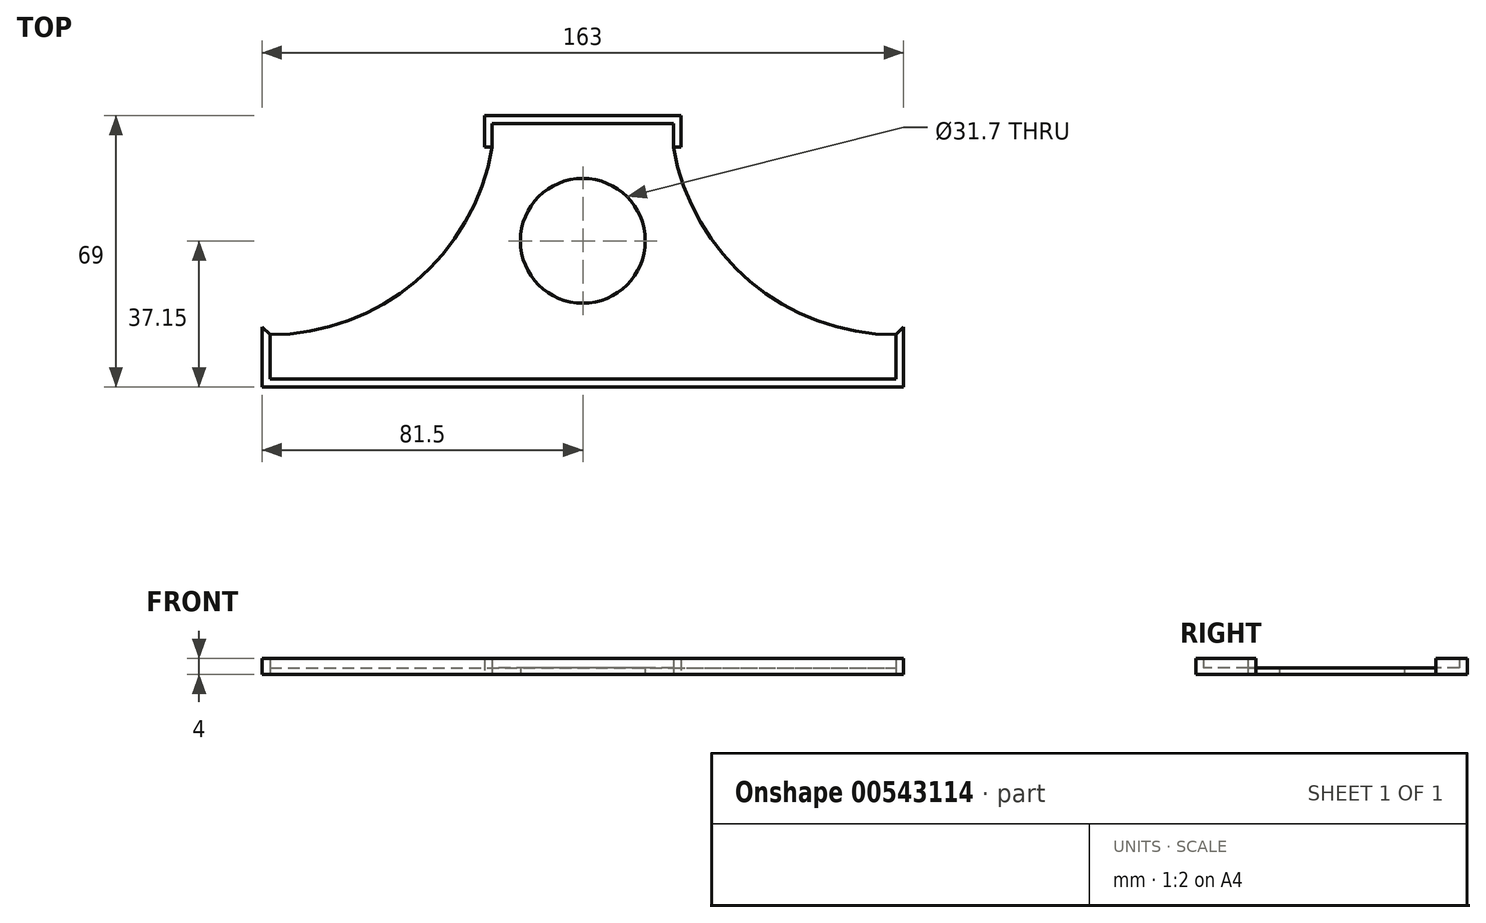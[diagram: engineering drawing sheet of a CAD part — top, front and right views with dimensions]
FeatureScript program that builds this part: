
annotation { "Feature Type Name" : "Feature", "Feature Type Description" : "" }
export const myFeature = defineFeature(function(context is Context, id is Id, definition is map)
    precondition{}
    {
        {
            var Q0;
            Q0=qCreatedBy(makeId("Top.planeOp"),FACE);
            var sketch = newSketch(context, id + "F0", { "sketchPlane" : qUnion([Q0])});
            skLineSegment(sketch, "E0", {"start": v(0, 0) * mm, "end": v(0, 5.65) * mm});
            skLineSegment(sketch, "E1", {"start": v(-79.5, 5.65) * mm, "end": v(79.5, 5.65) * mm});
            skLineSegment(sketch, "E2", {"start": v(-79.5, -5.65) * mm, "end": v(79.5, -5.65) * mm});
            skLineSegment(sketch, "E3", {"start": v(79.5, -5.65) * mm, "end": v(79.5, 5.65) * mm});
            skLineSegment(sketch, "E4", {"start": v(-79.5, 5.65) * mm, "end": v(-79.5, -5.65) * mm});
            skPoint(sketch, "E5", {"position": v(0, 59.35) * mm});
            skLineSegment(sketch, "E6", {"start": v(23, 59.35) * mm, "end": v(-23, 59.35) * mm});
            skLineSegment(sketch, "E7", {"start": v(-23, 53.35) * mm, "end": v(23, 53.35) * mm});
            skArc(sketch, "E8", {"start": v(-79.5, 5.65) * mm, "mid": v(-42.53, 19.17) * mm, "end": v(-23, 53.35) * mm});
            skArc(sketch, "E9", {"start": v(23, 53.35) * mm, "mid": v(42.53, 19.17) * mm, "end": v(79.5, 5.65) * mm});
            skLineSegment(sketch, "E10", {"start": v(-23, 59.35) * mm, "end": v(-23, 53.35) * mm});
            skLineSegment(sketch, "E11", {"start": v(23, 59.35) * mm, "end": v(23, 53.35) * mm});
            skLineSegment(sketch, "E12.0", {"start": v(23, 61.35) * mm, "end": v(-23, 61.35) * mm});
            skLineSegment(sketch, "E13", {"start": v(-23, 61.35) * mm, "end": v(-23, 59.35) * mm});
            skLineSegment(sketch, "E14", {"start": v(23, 61.35) * mm, "end": v(23, 59.35) * mm});
            skLineSegment(sketch, "E15.0", {"start": v(-25, 59.35) * mm, "end": v(-25, 53.35) * mm});
            skLineSegment(sketch, "E15.1", {"start": v(-25, 61.35) * mm, "end": v(-25, 59.35) * mm});
            skLineSegment(sketch, "E16.0", {"start": v(25, 59.35) * mm, "end": v(25, 53.35) * mm});
            skLineSegment(sketch, "E16.1", {"start": v(25, 61.35) * mm, "end": v(25, 59.35) * mm});
            skLineSegment(sketch, "E17", {"start": v(-25, 61.35) * mm, "end": v(-23, 61.35) * mm});
            skLineSegment(sketch, "E18", {"start": v(25, 61.35) * mm, "end": v(23, 61.35) * mm});
            skLineSegment(sketch, "E19.0", {"start": v(81.5, -7.65) * mm, "end": v(81.5, 7.66) * mm});
            skLineSegment(sketch, "E19.1", {"start": v(-81.5, -7.65) * mm, "end": v(81.5, -7.65) * mm});
            skLineSegment(sketch, "E19.2", {"start": v(-81.5, 7.66) * mm, "end": v(-81.5, -7.65) * mm});
            skLineSegment(sketch, "E20", {"start": v(-81.5, 7.66) * mm, "end": v(-79.5, 5.65) * mm});
            skLineSegment(sketch, "E21", {"start": v(79.5, 5.65) * mm, "end": v(81.5, 7.66) * mm});
            skPoint(sketch, "E22", {"position": v(0, 29.5) * mm});
            skPoint(sketch, "E22.positionSnap0", {"position": v(0, 53.35) * mm});
            skCircle(sketch, "E23", {"center": v(0, 29.5) * mm, "radius": 15.85 * mm});
            skArc(sketch, "E24", {"start": v(-81.5, 7.66) * mm, "mid": v(-44.7, 19.93) * mm, "end": v(-25, 53.35) * mm});
            skArc(sketch, "E25", {"start": v(25, 53.35) * mm, "mid": v(44.7, 19.93) * mm, "end": v(81.5, 7.66) * mm});
            skLineSegment(sketch, "E26", {"start": v(-25, 53.35) * mm, "end": v(-23, 53.35) * mm});
            skLineSegment(sketch, "E27", {"start": v(23, 53.35) * mm, "end": v(25, 53.35) * mm});
            skSolve(sketch);
        }
        {
            var Q0;
            Q0=makeQuery(id+"F0.imprint","IMPRINT",FACE,{"disambiguationData":[TD([[makeQuery(id+"F0.imprint","IMPRINT",EDGE,{"derivedFrom":sQuery(id+"F0.wireOp",EDGE,"E7")}),-1.0]])]});
            var Q1;
            Q1=makeQuery(id+"F0.imprint","IMPRINT",FACE,{"disambiguationData":[TD([[makeQuery(id+"F0.imprint","IMPRINT",EDGE,{"derivedFrom":sQuery(id+"F0.wireOp",EDGE,"E2")}),1.0]])]});
            var Q2;
            Q2=makeQuery(id+"F0.imprint","IMPRINT",FACE,{"disambiguationData":[TD([[makeQuery(id+"F0.imprint","IMPRINT",EDGE,{"derivedFrom":sQuery(id+"F0.wireOp",EDGE,"E6")}),1.0]])]});
            extrude(context, id + "F1", {"entities" : qUnion([Q0, Q1, Q2]), "depth" : 1.6 * mm, "offsetDistance" : 25 * mm});
        }
        {
            var Q0;
            Q0=makeQuery(id+"F0.imprint","IMPRINT",FACE,{"disambiguationData":[TD([[makeQuery(id+"F0.imprint","IMPRINT",EDGE,{"derivedFrom":sQuery(id+"F0.wireOp",EDGE,"E2")}),-1.0]])]});
            var Q1;
            Q1=makeQuery(id+"F0.imprint","IMPRINT",FACE,{"disambiguationData":[TD([[makeQuery(id+"F0.imprint","IMPRINT",EDGE,{"derivedFrom":sQuery(id+"F0.wireOp",EDGE,"E6")}),-1.0]])]});
            var Q2;
            Q2=makeQuery(id+"F0.imprint","IMPRINT",FACE,{"disambiguationData":[TD([[makeQuery(id+"F0.imprint","IMPRINT",EDGE,{"derivedFrom":sQuery(id+"F0.wireOp",EDGE,"E11")}),1.0]])]});
            var Q3;
            Q3=makeQuery(id+"F0.imprint","IMPRINT",FACE,{"disambiguationData":[TD([[makeQuery(id+"F0.imprint","IMPRINT",EDGE,{"derivedFrom":sQuery(id+"F0.wireOp",EDGE,"E10")}),-1.0]])]});
            extrude(context, id + "F2", {"entities" : qUnion([Q0, Q1, Q2, Q3]), "operationType" : NewBodyOperationType.ADD, "depth" : 4 * mm, "offsetDistance" : 25 * mm});
        }
    });
